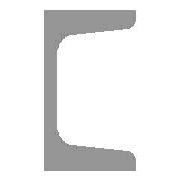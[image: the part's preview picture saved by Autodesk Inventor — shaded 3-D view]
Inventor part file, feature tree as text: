
AUTODESK INVENTOR PART (.ipt)
format: ipt  version: 2024 (Build 280153000, 153)  size: 138,240 bytes
history: native  units: mm (DEFAULTED — no unit token found)
features: other x3, extrude x1, sketch x1, plane x1
ambient origin geometry x8: Origin, YZ Plane, XZ Plane, XY Plane, X Axis, Y Axis, Z Axis, Center Point
bodies: Solid1 (feature_tree)
feature tree (6):
  other  "Driven Length"
  other  "Начальная плоскость"
  other  "Конечная плоскость"
  extrude  "Базовый элемент"  Depth=32.5mm
  sketch  "Sketch3"  dims[d0=5.5mm d1=32.5mm d2=42.0mm d3=7.5mm d4=21.0mm d5=1.68mm d6=30.0mm d7=0.0mm d23=7.5mm d24=4.0mm d25=0.0mm d26=-0.0mm d27=30.0mm d28=90.0deg d29=30.0mm]
  plane  "Work Plane3"
